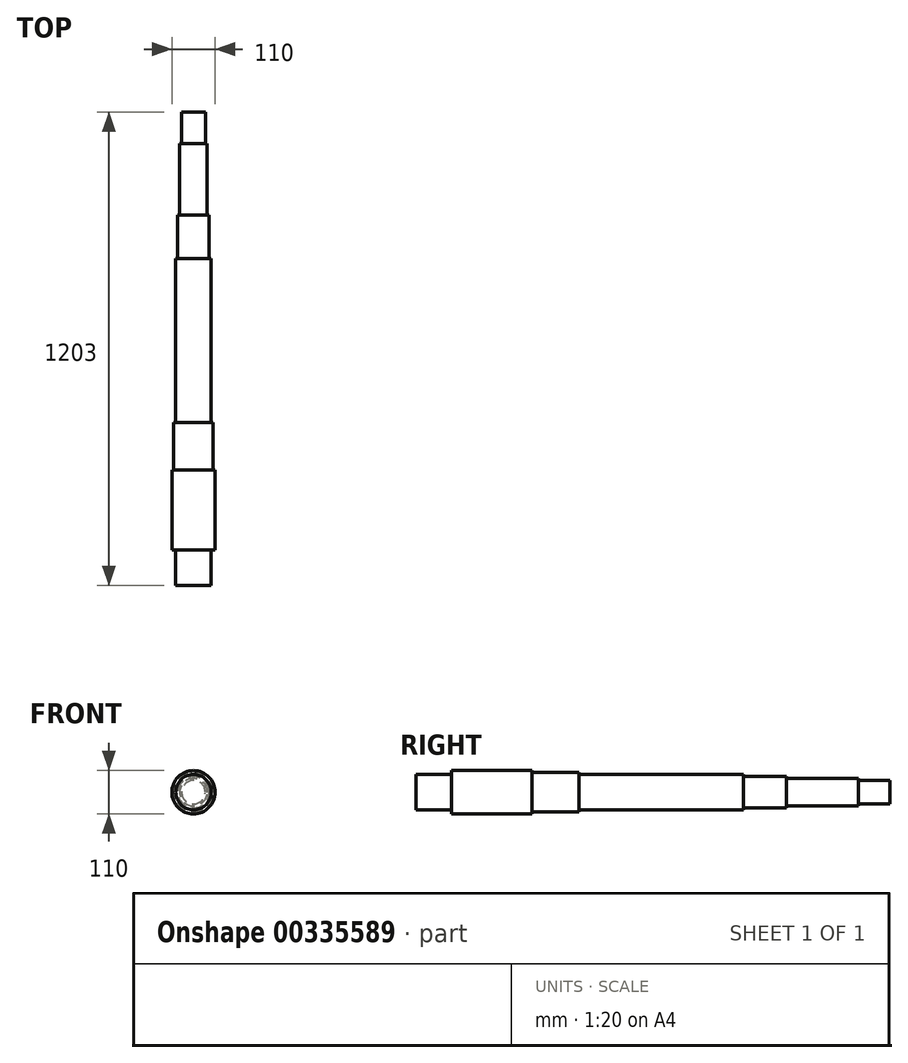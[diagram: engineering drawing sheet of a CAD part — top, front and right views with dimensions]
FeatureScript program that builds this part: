
annotation { "Feature Type Name" : "Feature", "Feature Type Description" : "" }
export const myFeature = defineFeature(function(context is Context, id is Id, definition is map)
    precondition{}
    {
        {
            var Q0;
            Q0=qCreatedBy(makeId("Front.planeOp"),FACE);
            var sketch = newSketch(context, id + "F0", { "sketchPlane" : qUnion([Q0])});
            skCircle(sketch, "E0", {"center": v(0, 0) * mm, "radius": 45 * mm});
            skSolve(sketch);
        }
        {
            var Q0;
            Q0=makeQuery(id+"F0.imprint","IMPRINT",FACE,{"disambiguationData":[TD([[makeQuery(id+"F0.imprint","IMPRINT",EDGE,{"derivedFrom":sQuery(id+"F0.wireOp",EDGE,"E0")}),1.0]])]});
            extrude(context, id + "F1", {"entities" : qUnion([Q0]), "oppositeDirection" : true, "depth" : 417 * mm});
        }
        {
            var Q0;
            Q0=makeQuery(id+"F1.opExtrude","CAP_FACE",FACE,{"disambiguationData":[OSD([sQuery(id+"F0.wireOp",EDGE,"E0")])],"isStart":false});
            var sketch = newSketch(context, id + "F2", { "sketchPlane" : qUnion([Q0])});
            skCircle(sketch, "E1", {"center": v(0, 0) * mm, "radius": 40 * mm});
            skSolve(sketch);
        }
        {
            var Q0;
            Q0=makeQuery(id+"F2.imprint","IMPRINT",FACE,{"disambiguationData":[TD([[makeQuery(id+"F2.imprint","IMPRINT",EDGE,{"derivedFrom":sQuery(id+"F2.wireOp",EDGE,"E1")}),1.0]])]});
            extrude(context, id + "F3", {"entities" : qUnion([Q0]), "operationType" : NewBodyOperationType.ADD, "depth" : 110 * mm});
        }
        {
            var Q0;
            Q0=makeQuery(id+"F3.opExtrude","CAP_FACE",FACE,{"disambiguationData":[OSD([sQuery(id+"F2.wireOp",EDGE,"E1")])],"isStart":false});
            var sketch = newSketch(context, id + "F4", { "sketchPlane" : qUnion([Q0])});
            skCircle(sketch, "E2", {"center": v(0, 0) * mm, "radius": 35 * mm});
            skSolve(sketch);
        }
        {
            var Q0;
            Q0=makeQuery(id+"F4.imprint","IMPRINT",FACE,{"disambiguationData":[TD([[makeQuery(id+"F4.imprint","IMPRINT",EDGE,{"derivedFrom":sQuery(id+"F4.wireOp",EDGE,"E2")}),1.0]])]});
            extrude(context, id + "F5", {"entities" : qUnion([Q0]), "operationType" : NewBodyOperationType.ADD, "depth" : 182 * mm});
        }
        {
            var Q0;
            Q0=makeQuery(id+"F5.opExtrude","CAP_FACE",FACE,{"disambiguationData":[OSD([sQuery(id+"F4.wireOp",EDGE,"E2")])],"isStart":false});
            var sketch = newSketch(context, id + "F6", { "sketchPlane" : qUnion([Q0])});
            skCircle(sketch, "E3", {"center": v(0, 0) * mm, "radius": 30 * mm});
            skSolve(sketch);
        }
        {
            var Q0;
            Q0=makeQuery(id+"F6.imprint","IMPRINT",FACE,{"disambiguationData":[TD([[makeQuery(id+"F6.imprint","IMPRINT",EDGE,{"derivedFrom":sQuery(id+"F6.wireOp",EDGE,"E3")}),1.0]])]});
            extrude(context, id + "F7", {"entities" : qUnion([Q0]), "operationType" : NewBodyOperationType.ADD, "depth" : 80 * mm});
        }
        {
            var Q0;
            Q0=makeQuery(id+"F1.opExtrude","CAP_FACE",FACE,{"disambiguationData":[OSD([sQuery(id+"F0.wireOp",EDGE,"E0")])],"isStart":true});
            var sketch = newSketch(context, id + "F8", { "sketchPlane" : qUnion([Q0])});
            skCircle(sketch, "E4", {"center": v(0, 0) * mm, "radius": 50 * mm});
            skSolve(sketch);
        }
        {
            var Q0;
            Q0 = qSketchRegion(id + "F8", true);
            extrude(context, id + "F9", {"entities" : qUnion([Q0]), "operationType" : NewBodyOperationType.ADD, "depth" : 120 * mm});
        }
        {
            var Q0;
            Q0=makeQuery(id+"F9.opExtrude","CAP_FACE",FACE,{"disambiguationData":[OSD([sQuery(id+"F8.wireOp",EDGE,"E4")])],"isStart":false});
            var sketch = newSketch(context, id + "F10", { "sketchPlane" : qUnion([Q0])});
            skCircle(sketch, "E5", {"center": v(0, 0) * mm, "radius": 55 * mm});
            skSolve(sketch);
        }
        {
            var Q0;
            Q0 = qSketchRegion(id + "F10", true);
            extrude(context, id + "F11", {"entities" : qUnion([Q0]), "operationType" : NewBodyOperationType.ADD, "depth" : 204 * mm});
        }
        {
            var Q0;
            Q0=makeQuery(id+"F11.opExtrude","CAP_FACE",FACE,{"disambiguationData":[OSD([sQuery(id+"F10.wireOp",EDGE,"E5")])],"isStart":false});
            var sketch = newSketch(context, id + "F12", { "sketchPlane" : qUnion([Q0])});
            skCircle(sketch, "E6", {"center": v(0, 0) * mm, "radius": 45 * mm});
            skSolve(sketch);
        }
        {
            var Q0;
            Q0 = qSketchRegion(id + "F12", true);
            extrude(context, id + "F13", {"entities" : qUnion([Q0]), "operationType" : NewBodyOperationType.ADD, "depth" : 90 * mm});
        }
    });
